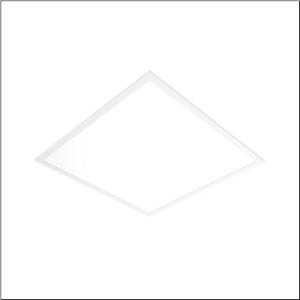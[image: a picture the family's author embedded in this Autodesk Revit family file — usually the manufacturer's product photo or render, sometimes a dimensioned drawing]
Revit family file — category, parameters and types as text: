
# Revit family: apollon_r__41_51mh12w72m43_b29b
name_source: partatom
category: Lighting Fixtures
units: mm (PartAtom-declared; Revit-internal decimal feet)

## family parameters
Cut with Voids When Loaded = No
Host = Face
Light Source = No
Part Type = Normal
Room Calculation Point = No
Round Connector Dimension = Use Diameter
Shared = No

## types (1)
- --- (1 x LED, 3700 lm, 28.5 W, 4000K)
    Apparent Load = 29 VA
    CIE Flux Codes = 61 87 97 100 100
    Color Rendering = 80
    Color Temperature = 4000K
    Default Elevation = 1800 mm
    Description = Apollon® 41, office luminaire, primary optical cover: prismatic diffuser, of PS, light emission: direct distribution, primary light characteristic: symmetric, installation type: lay-in mounting, LED, rated luminous flux: 3.700lm, luminous efficacy: 130lm/W, light colour: 830/840, colour temperature: 3000/4000K, with terminal, 3-pole, mains connection: 220..240V, AC, 50/60Hz, housing, of aluminium section, traffic white (RAL 9016), module: M600, length: 600mm, width: 600mm, height: 28mm, housing upper side, of sheet steel, protection rating (complete): IP20, protection rating (lamp compartment, on room side): IP40, insulation class (complete): insulation class II (safety insulation), certification: CE, ENEC, permissible operating ambient temperature: -25..+40°C, packaging unit: 1 piece
    Height = 0 mm  [stored 0 ft]
    Lamp = 1 x LED
    Lamp Light Flux = 3700 lm
    Lamp Power = 28.5 W
    Lamp count = 1
    Length = 600 mm
    Luminous efficacy = 130 lm/W
    Manufacturer = Siteco
    ModVariant = No
    Model = 51MH12W72M43
    Mounting Place = Ceiling
    Mounting Type = Recessed
    Number of Poles = 1
    OnlyDefault = Yes
    Power Factor = 1
    Product Name = Apollon® 41
    Product group = office luminaire | ceiling recessed
    ProductGroupID = 401
    Protection Class = Protection class II
    Protection Degree = IP 20
    RLX_Detail_Level = 1
    RLX_Emergency_Light_Flux = 0 lm
    RLX_Emergency_Type = 0
    RLX_Emergency_Type_DB = No
    RlxData = <blob elided: 12393 chars, md5=2397d680>
    Socket = socket
    Standby Power = 0 W
    System Light Flux = 3700 lm
    System Power = 29 W
    Type Comments = factory setting
    Type Image = l_1291024.jpg
    URL = http://relux.com
    VarID = @adj_008937
    Voltage = 0 V
    Weight = 0.00 kg
    Width = 600 mm

note: [stored X ft] marks values corroborated as IEEE doubles in the binary element streams (Revit-internal decimal feet)

## geometry (parser evidence)
native form markers: Sweep x10
no freeform markers — native parametric forms only
